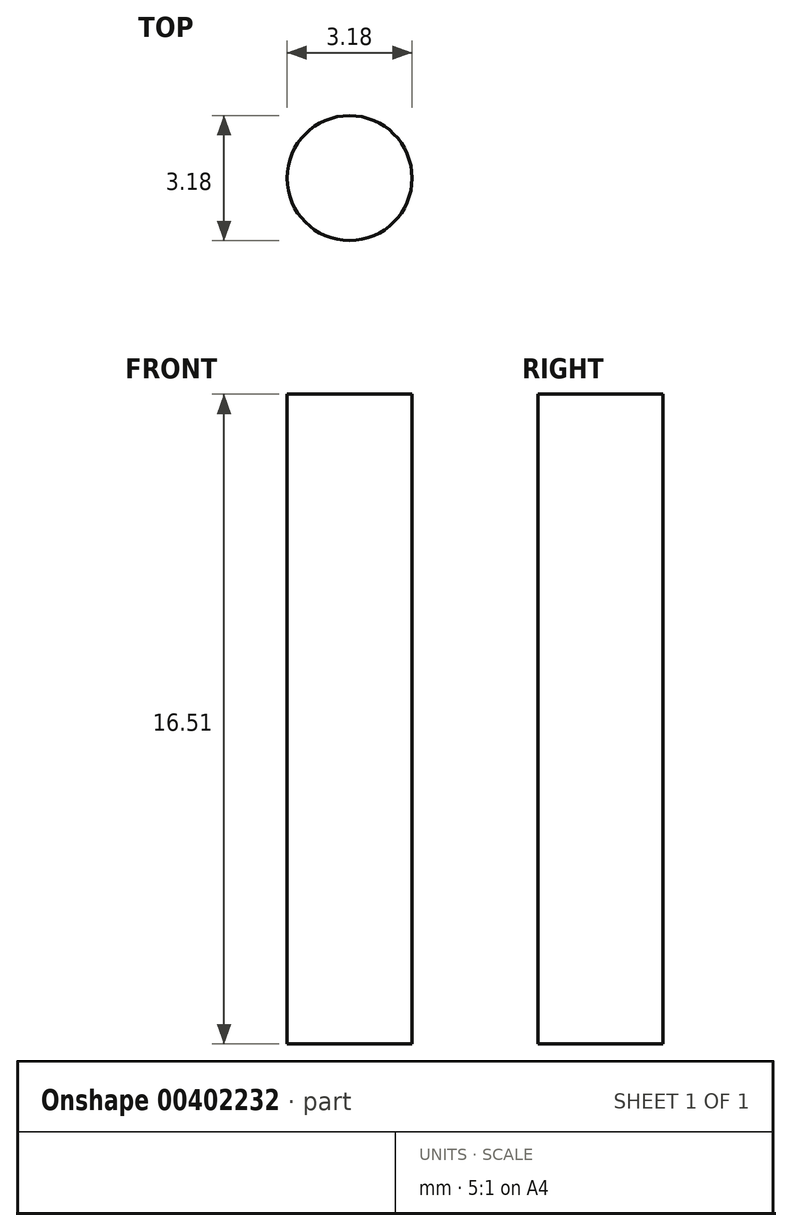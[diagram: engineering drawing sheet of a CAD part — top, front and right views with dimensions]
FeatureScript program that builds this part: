
annotation { "Feature Type Name" : "Feature", "Feature Type Description" : "" }
export const myFeature = defineFeature(function(context is Context, id is Id, definition is map)
    precondition{}
    {
        {
            var Q0;
            Q0=qCreatedBy(makeId("Top.planeOp"),FACE);
            var sketch = newSketch(context, id + "F0", { "sketchPlane" : qUnion([Q0])});
            skCircle(sketch, "E0", {"center": v(0, 0) * mm, "radius": 1.59 * mm});
            skSolve(sketch);
        }
        {
            var Q0;
            Q0 = qSketchRegion(id + "F0", true);
            extrude(context, id + "F1", {"entities" : qUnion([Q0]), "depth" : 16.5 * mm});
        }
    });
